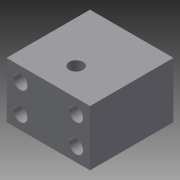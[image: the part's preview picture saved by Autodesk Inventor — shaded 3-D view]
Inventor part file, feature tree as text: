
AUTODESK INVENTOR PART (.ipt)
format: ipt  version: 2014 SP1 (Build 180222100, 222)  size: 94,720 bytes
history: native  units: in
note: dims shown in document units (in); Inventor stores cm internally (conversion verified against a paired STEP export)
features: sketch x3, hole x2, extrude x1
ambient origin geometry x8: Origin, YZ Plane, XZ Plane, XY Plane, X Axis, Y Axis, Z Axis, Center Point
bodies: Solid1 (feature_tree)
feature tree (6):
  extrude  "Extrusion1"  Depth=1.0in
  hole  "Hole1"  [1 undecoded]
  hole  "Hole2"  [1 undecoded]
  sketch  "Sketch1"  dims[d0=1.5in d1=1.0in]
  sketch  "Sketch2"  dims[d2=1.5in d3=0.0in d4=1.0in]
  sketch  "Sketch3"  dims[d5=0.5in d6=0.25in d7=0.75in d8=0.375in d9=0.25in d10=0.5635in d11=1.0in d12=0.8108in d13=1.0in d14=0.25in d15=0.75in d16=0.375in d17=0.25in d18=0.5635in d19=1.0in d20=0.8108in]
note: 2 required parameter values undecoded (feature->parameter linkage not recoverable at this tier; creation-order binding heuristic only, values carry confidence <= 0.55)
